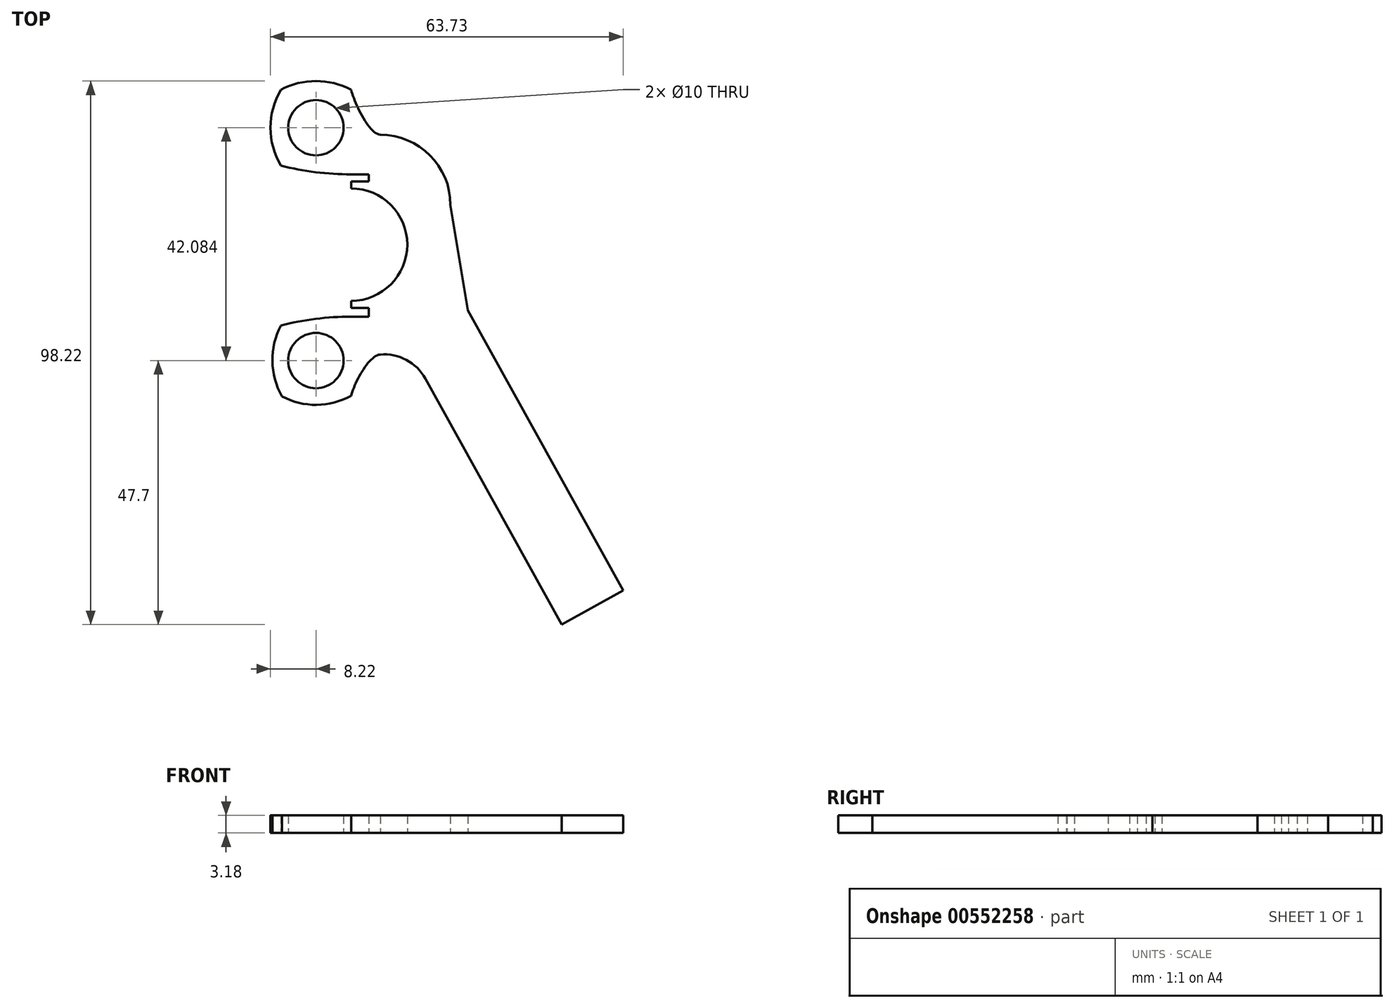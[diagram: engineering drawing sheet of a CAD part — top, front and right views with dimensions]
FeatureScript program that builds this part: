
annotation { "Feature Type Name" : "Feature", "Feature Type Description" : "" }
export const myFeature = defineFeature(function(context is Context, id is Id, definition is map)
    precondition{}
    {
        {
            var Q0;
            Q0=qCreatedBy(makeId("Top.planeOp"),FACE);
            var sketch = newSketch(context, id + "F0", { "sketchPlane" : qUnion([Q0])});
            skPoint(sketch, "E0.middle", {"position": v(0, 0) * mm});
            skArc(sketch, "E1", {"start": v(0, -12.06) * mm, "mid": v(10.16, -1.9) * mm, "end": v(0, 8.26) * mm});
            skPoint(sketch, "E2.visualSharp", {"position": v(17.96, 17.96) * mm});
            skArc(sketch, "E2.filletArc", {"start": v(17.96, 5.26) * mm, "mid": v(14.24, 14.24) * mm, "end": v(5.26, 17.96) * mm});
            skPoint(sketch, "E3.visualSharp", {"position": v(17.96, -17.96) * mm});
            skLineSegment(sketch, "E4", {"start": v(0, 8.26) * mm, "end": v(0, 9.53) * mm});
            skLineSegment(sketch, "E5", {"start": v(0, 9.53) * mm, "end": v(0, 9.53) * mm});
            skFitSpline(sketch, "E6", {"points": [v(0, 26.07) * mm, v(5.26, 17.96) * mm], "startDerivative": vector(2.09, -7.44) * mm, "endDerivative": vector(6.26, -0.53) * mm});
            skArc(sketch, "E7", {"start": v(-12.7, 26.07) * mm, "mid": v(-14.57, 19.22) * mm, "end": v(-12.7, 12.38) * mm});
            skArc(sketch, "E8", {"start": v(0, 26.07) * mm, "mid": v(-6.35, 27.66) * mm, "end": v(-12.7, 26.07) * mm});
            skPoint(sketch, "E9.middle", {"position": v(0, -3.8) * mm});
            skPoint(sketch, "E10.visualSharp", {"position": v(-17.96, -21.77) * mm});
            skPoint(sketch, "E11.visualSharp", {"position": v(-17.96, 14.15) * mm});
            skLineSegment(sketch, "E12", {"start": v(0, -12.06) * mm, "end": v(0, -13.33) * mm});
            skLineSegment(sketch, "E13.MirrorCS", {"start": v(0, -13.33) * mm, "end": v(0, -13.33) * mm});
            skArc(sketch, "E14.MirrorCS", {"start": v(-12.5, -29.32) * mm, "mid": v(-14.22, -22.94) * mm, "end": v(-12.7, -16.5) * mm});
            skArc(sketch, "E15.MirrorCS", {"start": v(0, -29.2) * mm, "mid": v(-6.23, -30.87) * mm, "end": v(-12.5, -29.32) * mm});
            skFitSpline(sketch, "E16.MirrorCS", {"points": [v(0, -29.2) * mm, v(5.26, -21.77) * mm], "startDerivative": vector(2.09, 7.44) * mm, "endDerivative": vector(6.26, 0.53) * mm});
            skLineSegment(sketch, "E17", {"start": v(0, -13.33) * mm, "end": v(3.17, -13.33) * mm});
            skLineSegment(sketch, "E18.bottom", {"start": v(3.17, -13.33) * mm, "end": v(0, -13.33) * mm});
            skLineSegment(sketch, "E18.top", {"start": v(3.17, -14.92) * mm, "end": v(0, -14.92) * mm});
            skLineSegment(sketch, "E18.left", {"start": v(3.17, -13.33) * mm, "end": v(3.17, -14.92) * mm});
            skArc(sketch, "E19", {"start": v(0, -14.92) * mm, "mid": v(-6.4, -15.32) * mm, "end": v(-12.7, -16.5) * mm});
            skCircle(sketch, "E20", {"center": v(-6.35, -22.86) * mm, "radius": 5 * mm});
            skLineSegment(sketch, "E21", {"start": v(0, 9.53) * mm, "end": v(3.17, 9.53) * mm});
            skLineSegment(sketch, "E22.bottom", {"start": v(3.17, 9.53) * mm, "end": v(0, 9.53) * mm});
            skLineSegment(sketch, "E22.top", {"start": v(3.18, 10.8) * mm, "end": v(0, 10.8) * mm});
            skLineSegment(sketch, "E22.left", {"start": v(3.17, 9.53) * mm, "end": v(3.17, 10.8) * mm});
            skArc(sketch, "E23", {"start": v(-12.7, 12.38) * mm, "mid": v(-6.4, 11.2) * mm, "end": v(0, 10.8) * mm});
            skCircle(sketch, "E24", {"center": v(-6.35, 19.22) * mm, "radius": 5 * mm});
            skLineSegment(sketch, "E25", {"start": v(13.43, -26.13) * mm, "end": v(38.05, -70.56) * mm});
            skLineSegment(sketch, "E26", {"start": v(38.05, -70.56) * mm, "end": v(49.16, -64.4) * mm});
            skLineSegment(sketch, "E27", {"start": v(49.16, -64.4) * mm, "end": v(21.1, -13.78) * mm});
            skArc(sketch, "E28", {"start": v(13.43, -26.13) * mm, "mid": v(9.99, -22.74) * mm, "end": v(5.26, -21.77) * mm});
            skLineSegment(sketch, "E29", {"start": v(17.96, 5.26) * mm, "end": v(21.1, -13.78) * mm});
            skSolve(sketch);
        }
        {
            var Q0;
            Q0=makeQuery(id+"F0.imprint","IMPRINT",FACE,{"disambiguationData":[TD([[makeQuery(id+"F0.imprint","IMPRINT",EDGE,{"derivedFrom":sQuery(id+"F0.wireOp",EDGE,"E1")}),-1.0]])]});
            extrude(context, id + "F1", {"entities" : qUnion([Q0]), "depth" : 3.17 * mm, "offsetDistance" : 25.4 * mm});
        }
    });
